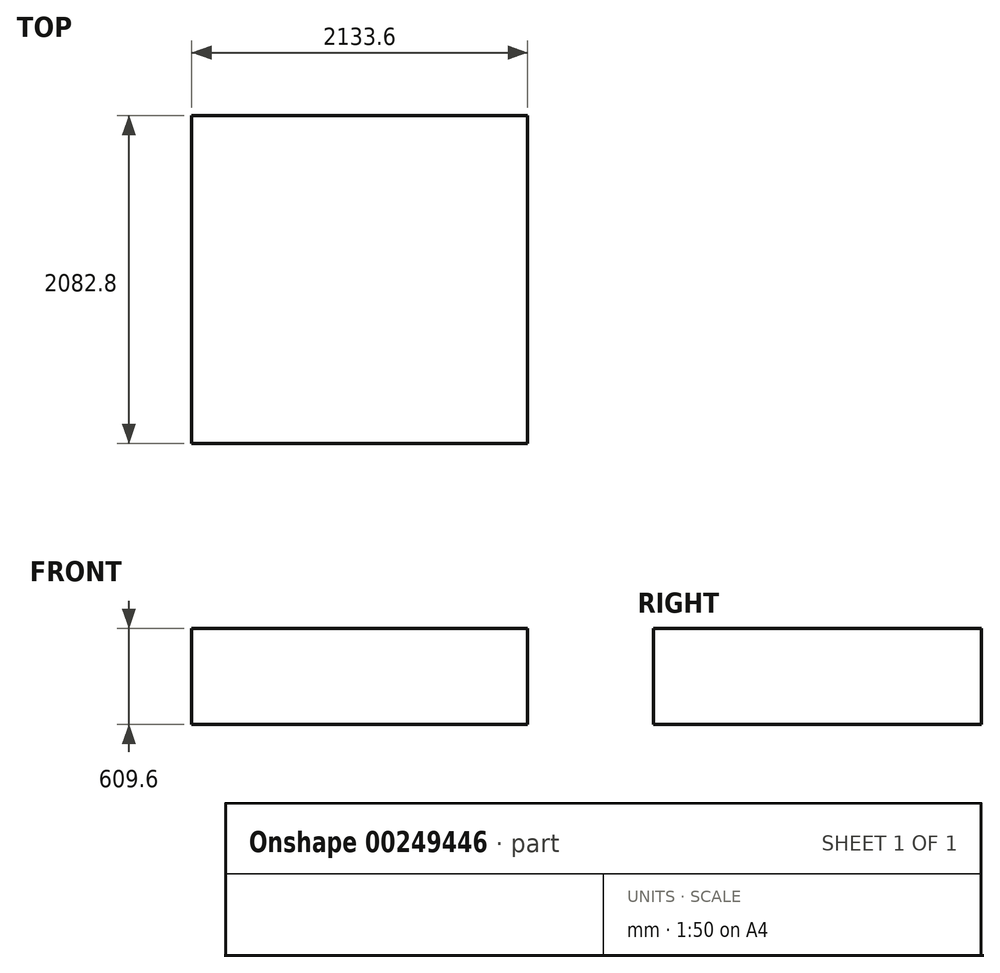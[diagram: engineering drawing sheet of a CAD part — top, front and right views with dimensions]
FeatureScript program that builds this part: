
annotation { "Feature Type Name" : "Feature", "Feature Type Description" : "" }
export const myFeature = defineFeature(function(context is Context, id is Id, definition is map)
    precondition{}
    {
        {
            var Q0;
            Q0=qCreatedBy(makeId("Top.planeOp"),FACE);
            var sketch = newSketch(context, id + "F0", { "sketchPlane" : qUnion([Q0])});
            skLineSegment(sketch, "E0.bottom", {"start": v(1066.8, 1041.4) * mm, "end": v(-1066.8, 1041.4) * mm});
            skLineSegment(sketch, "E0.top", {"start": v(1066.8, -1041.4) * mm, "end": v(-1066.8, -1041.4) * mm});
            skLineSegment(sketch, "E0.left", {"start": v(1066.8, 1041.4) * mm, "end": v(1066.8, -1041.4) * mm});
            skLineSegment(sketch, "E0.right", {"start": v(-1066.8, 1041.4) * mm, "end": v(-1066.8, -1041.4) * mm});
            skPoint(sketch, "E0.middle", {"position": v(0, 0) * mm});
            skSolve(sketch);
        }
        {
            var Q0;
            Q0 = qSketchRegion(id + "F0", true);
            extrude(context, id + "F1", {"entities" : qUnion([Q0]), "depth" : 609.6 * mm});
        }
    });
